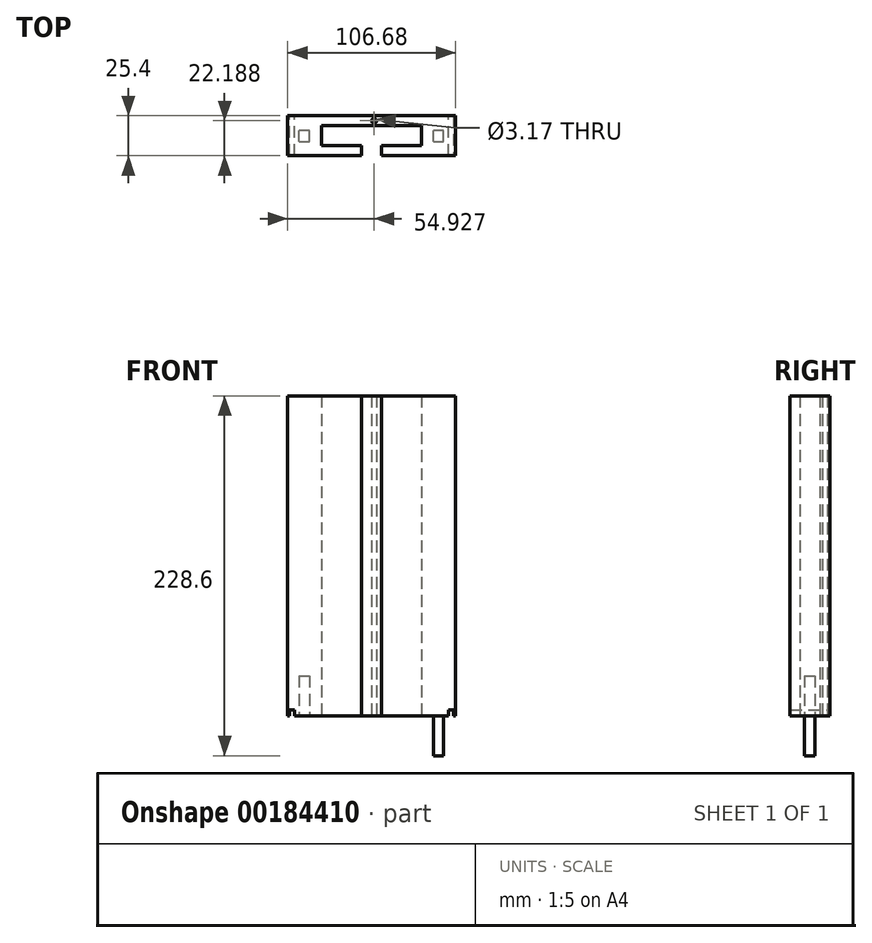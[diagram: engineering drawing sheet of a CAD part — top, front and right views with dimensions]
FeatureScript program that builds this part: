
annotation { "Feature Type Name" : "Feature", "Feature Type Description" : "" }
export const myFeature = defineFeature(function(context is Context, id is Id, definition is map)
    precondition{}
    {
        {
            var Q0;
            Q0=qCreatedBy(makeId("Top.planeOp"),FACE);
            var sketch = newSketch(context, id + "F0", { "sketchPlane" : qUnion([Q0])});
            skLineSegment(sketch, "E0", {"start": v(-59.7, 34.3) * mm, "end": v(47, 34.3) * mm});
            skLineSegment(sketch, "E1", {"start": v(-59.7, 34.3) * mm, "end": v(-59.69, 8.9) * mm});
            skLineSegment(sketch, "E2", {"start": v(47, 34.3) * mm, "end": v(47, 8.9) * mm});
            skLineSegment(sketch, "E3", {"start": v(-59.69, 8.9) * mm, "end": v(-12.7, 8.9) * mm});
            skLineSegment(sketch, "E4", {"start": v(-12.7, 8.9) * mm, "end": v(-12.7, 15.24) * mm});
            skLineSegment(sketch, "E5", {"start": v(-12.7, 15.24) * mm, "end": v(-38.1, 15.24) * mm});
            skLineSegment(sketch, "E6", {"start": v(-38.1, 15.24) * mm, "end": v(-38.1, 27.94) * mm});
            skLineSegment(sketch, "E7", {"start": v(-38.1, 27.94) * mm, "end": v(25.4, 27.94) * mm});
            skLineSegment(sketch, "E8", {"start": v(25.4, 27.94) * mm, "end": v(25.4, 15.24) * mm});
            skLineSegment(sketch, "E9", {"start": v(25.4, 15.24) * mm, "end": v(0, 15.24) * mm});
            skLineSegment(sketch, "E10", {"start": v(0, 15.24) * mm, "end": v(0, 8.9) * mm});
            skLineSegment(sketch, "E11", {"start": v(0, 8.9) * mm, "end": v(47, 8.9) * mm});
            skCircle(sketch, "E12", {"center": v(-4.76, 31.08) * mm, "radius": 1.59 * mm});
            skSolve(sketch);
        }
        {
            var Q0;
            Q0 = qSketchRegion(id + "F0", true);
            extrude(context, id + "F1", {"entities" : qUnion([Q0]), "depth" : 203.2 * mm});
        }
        {
            var Q0;
            Q0=makeQuery(id+"F1.opExtrude","SWEPT_FACE",FACE,{"disambiguationData":[OSD([sQuery(id+"F0.wireOp",EDGE,"E0")])]});
            var sketch = newSketch(context, id + "F2", { "sketchPlane" : qUnion([Q0])});
            skLineSegment(sketch, "E13", {"start": v(54.61, 207.65) * mm, "end": v(58.42, 207.65) * mm});
            skLineSegment(sketch, "E14", {"start": v(58.42, 198.76) * mm, "end": v(54.61, 198.76) * mm});
            skLineSegment(sketch, "E15", {"start": v(54.61, 198.76) * mm, "end": v(54.61, 207.65) * mm});
            skLineSegment(sketch, "E16", {"start": v(58.42, 207.65) * mm, "end": v(58.42, 198.76) * mm});
            skSolve(sketch);
        }
        {
            var Q0;
            Q0=makeQuery(id+"F2.imprint","IMPRINT",FACE,{"disambiguationData":[TD([[makeQuery(id+"F2.imprint","IMPRINT",EDGE,{"derivedFrom":sQuery(id+"F2.wireOp",EDGE,"E13")}),-1.0]])]});
            extrude(context, id + "F3", {"entities" : qUnion([Q0]), "operationType" : NewBodyOperationType.REMOVE, "oppositeDirection" : true, "depth" : 25.4 * mm});
        }
        {
            var Q0;
            Q0=makeQuery(id+"F1.opExtrude","SWEPT_FACE",FACE,{"disambiguationData":[OSD([sQuery(id+"F0.wireOp",EDGE,"E0")])]});
            var sketch = newSketch(context, id + "F4", { "sketchPlane" : qUnion([Q0])});
            skLineSegment(sketch, "E17", {"start": v(-45.72, 207.64) * mm, "end": v(-41.9, 207.64) * mm});
            skLineSegment(sketch, "E18", {"start": v(-45.72, 207.64) * mm, "end": v(-45.72, 198.76) * mm});
            skLineSegment(sketch, "E19", {"start": v(-45.72, 198.76) * mm, "end": v(-41.95, 198.76) * mm});
            skLineSegment(sketch, "E20", {"start": v(-41.95, 198.76) * mm, "end": v(-41.9, 207.64) * mm});
            skSolve(sketch);
        }
        {
            var Q0;
            Q0=makeQuery(id+"F4.imprint","IMPRINT",FACE,{"disambiguationData":[TD([[makeQuery(id+"F4.imprint","IMPRINT",EDGE,{"derivedFrom":sQuery(id+"F4.wireOp",EDGE,"E17")}),-1.0]])]});
            extrude(context, id + "F5", {"entities" : qUnion([Q0]), "operationType" : NewBodyOperationType.REMOVE, "oppositeDirection" : true, "depth" : 25.4 * mm});
        }
        {
            var Q0;
            Q0=makeQuery(id+"F1.opExtrude","CAP_FACE",FACE,{"disambiguationData":[OSD([sQuery(id+"F0.wireOp",EDGE,"E0"),sQuery(id+"F0.wireOp",EDGE,"E1"),sQuery(id+"F0.wireOp",EDGE,"E2"),sQuery(id+"F0.wireOp",EDGE,"E3"),sQuery(id+"F0.wireOp",EDGE,"E4"),sQuery(id+"F0.wireOp",EDGE,"E5"),sQuery(id+"F0.wireOp",EDGE,"E6"),sQuery(id+"F0.wireOp",EDGE,"E7"),sQuery(id+"F0.wireOp",EDGE,"E8"),sQuery(id+"F0.wireOp",EDGE,"E9"),sQuery(id+"F0.wireOp",EDGE,"E10"),sQuery(id+"F0.wireOp",EDGE,"E11"),sQuery(id+"F0.wireOp",EDGE,"E12")])],"isStart":true});
            var sketch = newSketch(context, id + "F6", { "sketchPlane" : qUnion([Q0])});
            skLineSegment(sketch, "E21", {"start": v(-52.58, -17.9) * mm, "end": v(-45.72, -17.9) * mm});
            skLineSegment(sketch, "E22", {"start": v(-52.58, -17.9) * mm, "end": v(-52.58, -24.77) * mm});
            skLineSegment(sketch, "E23", {"start": v(-45.72, -17.9) * mm, "end": v(-45.72, -24.77) * mm});
            skLineSegment(sketch, "E24", {"start": v(-45.72, -24.77) * mm, "end": v(-52.58, -24.77) * mm});
            skLineSegment(sketch, "E25", {"start": v(33.02, -17.9) * mm, "end": v(39.37, -17.9) * mm});
            skLineSegment(sketch, "E26", {"start": v(39.37, -17.9) * mm, "end": v(39.37, -24.77) * mm});
            skLineSegment(sketch, "E27", {"start": v(39.37, -24.77) * mm, "end": v(33.02, -24.77) * mm});
            skLineSegment(sketch, "E28", {"start": v(33.02, -17.9) * mm, "end": v(33.02, -24.77) * mm});
            skSolve(sketch);
        }
        {
            var Q0;
            Q0=makeQuery(id+"F6.imprint","IMPRINT",FACE,{"disambiguationData":[TD([[makeQuery(id+"F6.imprint","IMPRINT",EDGE,{"derivedFrom":sQuery(id+"F6.wireOp",EDGE,"E21")}),-1.0]])]});
            extrude(context, id + "F7", {"entities" : qUnion([Q0]), "operationType" : NewBodyOperationType.REMOVE, "oppositeDirection" : true, "depth" : 25.4 * mm});
        }
        {
            var Q0;
            Q0=makeQuery(id+"F6.imprint","IMPRINT",FACE,{"disambiguationData":[TD([[makeQuery(id+"F6.imprint","IMPRINT",EDGE,{"derivedFrom":sQuery(id+"F6.wireOp",EDGE,"E25")}),-1.0]])]});
            extrude(context, id + "F8", {"entities" : qUnion([Q0]), "operationType" : NewBodyOperationType.ADD, "depth" : 25.4 * mm});
        }
        {
            var Q0;
            Q0=makeQuery(id+"F1.opExtrude","CAP_FACE",FACE,{"disambiguationData":[OSD([sQuery(id+"F0.wireOp",EDGE,"E0"),sQuery(id+"F0.wireOp",EDGE,"E1"),sQuery(id+"F0.wireOp",EDGE,"E2"),sQuery(id+"F0.wireOp",EDGE,"E3"),sQuery(id+"F0.wireOp",EDGE,"E4"),sQuery(id+"F0.wireOp",EDGE,"E5"),sQuery(id+"F0.wireOp",EDGE,"E6"),sQuery(id+"F0.wireOp",EDGE,"E7"),sQuery(id+"F0.wireOp",EDGE,"E8"),sQuery(id+"F0.wireOp",EDGE,"E9"),sQuery(id+"F0.wireOp",EDGE,"E10"),sQuery(id+"F0.wireOp",EDGE,"E11"),sQuery(id+"F0.wireOp",EDGE,"E12")])],"isStart":true});
            var sketch = newSketch(context, id + "F9", { "sketchPlane" : qUnion([Q0])});
            skLineSegment(sketch, "E29", {"start": v(-58.42, -8.9) * mm, "end": v(-58.42, -34.3) * mm});
            skLineSegment(sketch, "E30", {"start": v(-55.25, -8.9) * mm, "end": v(-55.25, -34.3) * mm});
            skSolve(sketch);
        }
        {
            var Q0;
            {var subQ0=sQuery(id+"F9.wireOp",EDGE,"E29");Q0=makeQuery(id+"F9.imprint","IMPRINT",FACE,{"disambiguationData":[TD([[makeQuery(id+"F9.imprint","IMPRINT",EDGE,{"derivedFrom":subQ0}),1.0]])]});}
            extrude(context, id + "F10", {"entities" : qUnion([Q0]), "operationType" : NewBodyOperationType.REMOVE, "oppositeDirection" : true, "depth" : 3.8 * mm});
        }
        {
            var Q0;
            {var subQ0=sQuery(id+"F0.wireOp",EDGE,"E9");var subQ1=sQuery(id+"F0.wireOp",EDGE,"E8");var subQ2=sQuery(id+"F0.wireOp",EDGE,"E7");var subQ3=sQuery(id+"F0.wireOp",EDGE,"E6");var subQ4=sQuery(id+"F0.wireOp",EDGE,"E5");var subQ5=sQuery(id+"F0.wireOp",EDGE,"E0");var subQ6=sQuery(id+"F0.wireOp",EDGE,"E2");var subQ7=sQuery(id+"F0.wireOp",EDGE,"E10");var subQ8=sQuery(id+"F0.wireOp",EDGE,"E3");var subQ9=sQuery(id+"F0.wireOp",EDGE,"E4");var subQ10=sQuery(id+"F0.wireOp",EDGE,"E11");var subQ11=sQuery(id+"F0.wireOp",EDGE,"E12");Q0=makeQuery(id+"F10.boolean.opBoolean","SPLIT",FACE,{"disambiguationData":[TD([makeQuery(id+"F1.opExtrude","SWEPT_FACE",FACE,{"disambiguationData":[OSD([subQ6])]})])],"derivedFrom":makeQuery(id+"F1.opExtrude","CAP_FACE",FACE,{"disambiguationData":[OSD([subQ5,sQuery(id+"F0.wireOp",EDGE,"E1"),subQ6,subQ8,subQ9,subQ4,subQ3,subQ2,subQ1,subQ0,subQ7,subQ10,subQ11])],"isStart":true})});}
            var sketch = newSketch(context, id + "F11", { "sketchPlane" : qUnion([Q0])});
            skLineSegment(sketch, "E31", {"start": v(42.55, -8.9) * mm, "end": v(42.55, -34.3) * mm});
            skLineSegment(sketch, "E32", {"start": v(42.55, -34.3) * mm, "end": v(47, -34.3) * mm});
            skLineSegment(sketch, "E33", {"start": v(45.72, -34.3) * mm, "end": v(45.72, -8.9) * mm});
            skSolve(sketch);
        }
        {
            var Q0;
            {var subQ0=sQuery(id+"F11.wireOp",EDGE,"E31");Q0=makeQuery(id+"F11.imprint","IMPRINT",FACE,{"disambiguationData":[TD([[makeQuery(id+"F11.imprint","IMPRINT",EDGE,{"derivedFrom":subQ0}),1.0]])]});}
            extrude(context, id + "F12", {"entities" : qUnion([Q0]), "operationType" : NewBodyOperationType.REMOVE, "oppositeDirection" : true, "depth" : 3.8 * mm});
        }
    });
